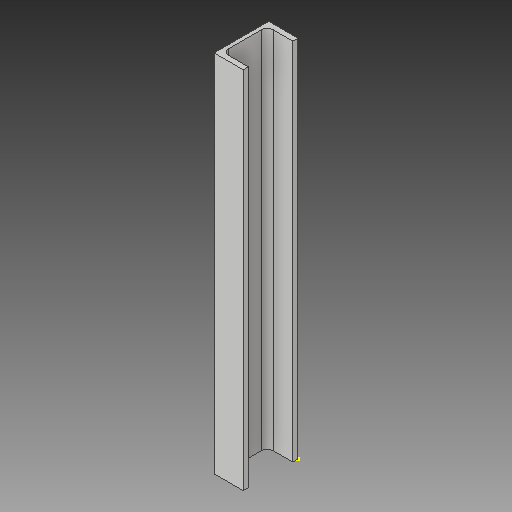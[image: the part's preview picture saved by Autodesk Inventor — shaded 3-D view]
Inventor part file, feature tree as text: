
AUTODESK INVENTOR PART (.ipt)
format: ipt  version: 2019 (Build 230136000, 136)  size: 97,280 bytes
history: native  units: in
note: dims shown in document units (in); Inventor stores cm internally (conversion verified against a paired STEP export)
features: other x3, sketch x2
ambient origin geometry x8: Origin, YZ Plane, XZ Plane, XY Plane, X Axis, Y Axis, Z Axis, Center Point
bodies: Solid1 (feature_tree)
feature tree (5):
  other  "Channel2.ipt"
  other  "Solid1::Channel2.ipt"
  other  "TaggingFeature1"
  sketch  "Sketch1"  dims[d0=0.3937in]
  sketch  "Sketch2"
